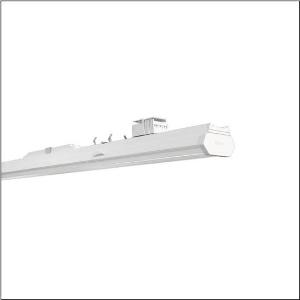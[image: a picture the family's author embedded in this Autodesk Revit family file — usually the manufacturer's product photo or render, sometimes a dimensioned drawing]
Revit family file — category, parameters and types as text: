
# Revit family: licross_r__21_protected_mo_52td12dn4a5g3s_ad63
name_source: partatom
category: Lighting Fixtures
units: mm (PartAtom-declared; Revit-internal decimal feet)

## family parameters
Cut with Voids When Loaded = No
Host = Face
Light Source = No
Part Type = Normal
Room Calculation Point = No
Round Connector Dimension = Use Diameter
Shared = No

## types (1)
- --- (1 x LED, 940 lm, 6.8 W, 4000K)
    Apparent Load = 7 VA
    CIE Flux Codes = 73 92 98 99 100
    Color Rendering = 80
    Color Temperature = 4000K
    Default Elevation = 1800 mm
    Description = Licross® 21 Protected MO, luminaire insert, of sheet steel, galvanised, coil coated, white, length: 1.500mm, width: 90mm, height: 103mm, LED rated luminous flux: 10.700lm, light colour: 840, SDCM (Standard Deviation of Colour Matching)MacAdam ≤ 3 SDCM (initial), control gear: DALI 2 (for two DALI lines), with plug, 6-pole, with phase selection, for trunking rail, 14-core, mains connection: 220..240V, AC, 50/60Hz, rated input power: 66W, for trunking rail, 14-core, internal wiring halogen-free, for emergency light function, converter,control gear: single battery element, battery: LiFePO4, 9Ah, primary light control with lens, of plastic, primary optical cover: cover, of PMMA, light emission: direct distribution, primary light characteristic: symmetric, protection rating (complete): IP54, insulation class (complete): insulation class I (protective earthing), certification: CE, UKCA, protection symbol: D if used in an environment with non-conductive dust loads with corresponding accessories, impact resistance: IK06, permissible ambient temperature for indoor applications: +5..+35°C, standard: EN 60598-2-22, LABS conformity tested according to VDMA 24364:2018-05, reducing of maximum allowable ambient temperature of 5°C with ceiling mounting, corresponds to IFS (International Featured Standards) requirements for safety and quality in the food industry, packaging unit: 1 piece
    Height = 92 mm
    Lamp = 1 x LED
    Lamp Light Flux = 940 lm
    Lamp Power = 6.8 W
    Lamp count = 1
    Length = 1500 mm
    Luminous efficacy = 138 lm/W
    Manufacturer = Siteco
    ModVariant = No
    Model = 52TD12DN4A5G3S
    Mounting Place = Ceiling
    Mounting Type = Pendant
    Number of Poles = 1
    OnlyDefault = Yes
    Power Factor = 1
    Product Name = Licross® 21 Protected MO
    Product group = luminaire insert | ceiling pendant
    ProductGroupID = 901
    Protection Class = Protection class I
    Protection Degree = IP 54
    RLX_Detail_Level = 1
    RLX_Emergency_Light_Flux = 0 lm
    RLX_Emergency_Type = 0
    RLX_Emergency_Type_DB = No
    RlxData = <blob elided: 24937 chars, md5=f0f8e9dd>
    Socket = socket
    Standby Power = 0 W
    System Light Flux = 940 lm
    System Power = 7 W
    Type Comments = : emergency light operation: 3 h
    Type Image = l_1256148.jpg
    URL = http://relux.com
    VarID = @adj_114841
    Voltage = 0 V
    Weight = 0.00 kg
    Width = 88 mm

## geometry (parser evidence)
native form markers: Blend x4, Sweep x9
no freeform markers — native parametric forms only
